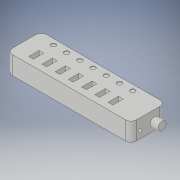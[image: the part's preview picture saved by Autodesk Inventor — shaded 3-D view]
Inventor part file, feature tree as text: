
AUTODESK INVENTOR PART (.ipt)
format: ipt  version: 2019 (Build 230136000, 136)  size: 213,504 bytes
history: native  units: mm
features: extrude x6, sketch x6, fillet x1
ambient origin geometry x8: Origin, YZ Plane, XZ Plane, XY Plane, X Axis, Y Axis, Z Axis, Center Point
bodies: Solid1 (feature_tree)
feature tree (13):
  extrude  "Extrusion1"  Depth=160.5mm
  fillet  "Fillet1"  Radius=23.6mm
  extrude  "Extrusion2"  Depth=7.2mm
  extrude  "Extrusion3"  Depth=13.6mm
  extrude  "Extrusion4"  Depth=10.0mm
  extrude  "Extrusion5"  Depth=19.6mm
  extrude  "Extrusion6"  Depth=7.35mm
  sketch  "Sketch1"  dims[d0=44.5mm d1=160.5mm d2=23.6mm d3=0.0mm]
  sketch  "Sketch2"  dims[d4=7.2mm d5=4.5mm]
  sketch  "Sketch3"  dims[d7=13.6mm d8=11.5mm]
  sketch  "Sketch4"  dims[d9=10.0mm d10=0.0mm d11=10.6mm]
  sketch  "Sketch5"  dims[d12=15.6mm d13=19.6mm]
  sketch  "Sketch6"  dims[d14=10.0mm d15=0.0mm d16=7.35mm d17=6.8mm d18=13.5mm d19=15.5mm d20=15.5mm d21=20.0mm d22=0.0mm d23=42.9mm d24=158.8mm d25=0.8mm d27=0.8mm d28=0.85mm d29=0.85mm d30=7.55mm d31=13.5mm d32=6.2mm d33=19.0mm d34=70.0mm d36=17.1mm d37=10.0mm d39=10.0mm d41=10.0mm d42=0.0mm d43=4.2mm d44=70.0mm d46=17.1mm d47=10.0mm d49=10.0mm d51=1.0mm d52=0.0mm]
